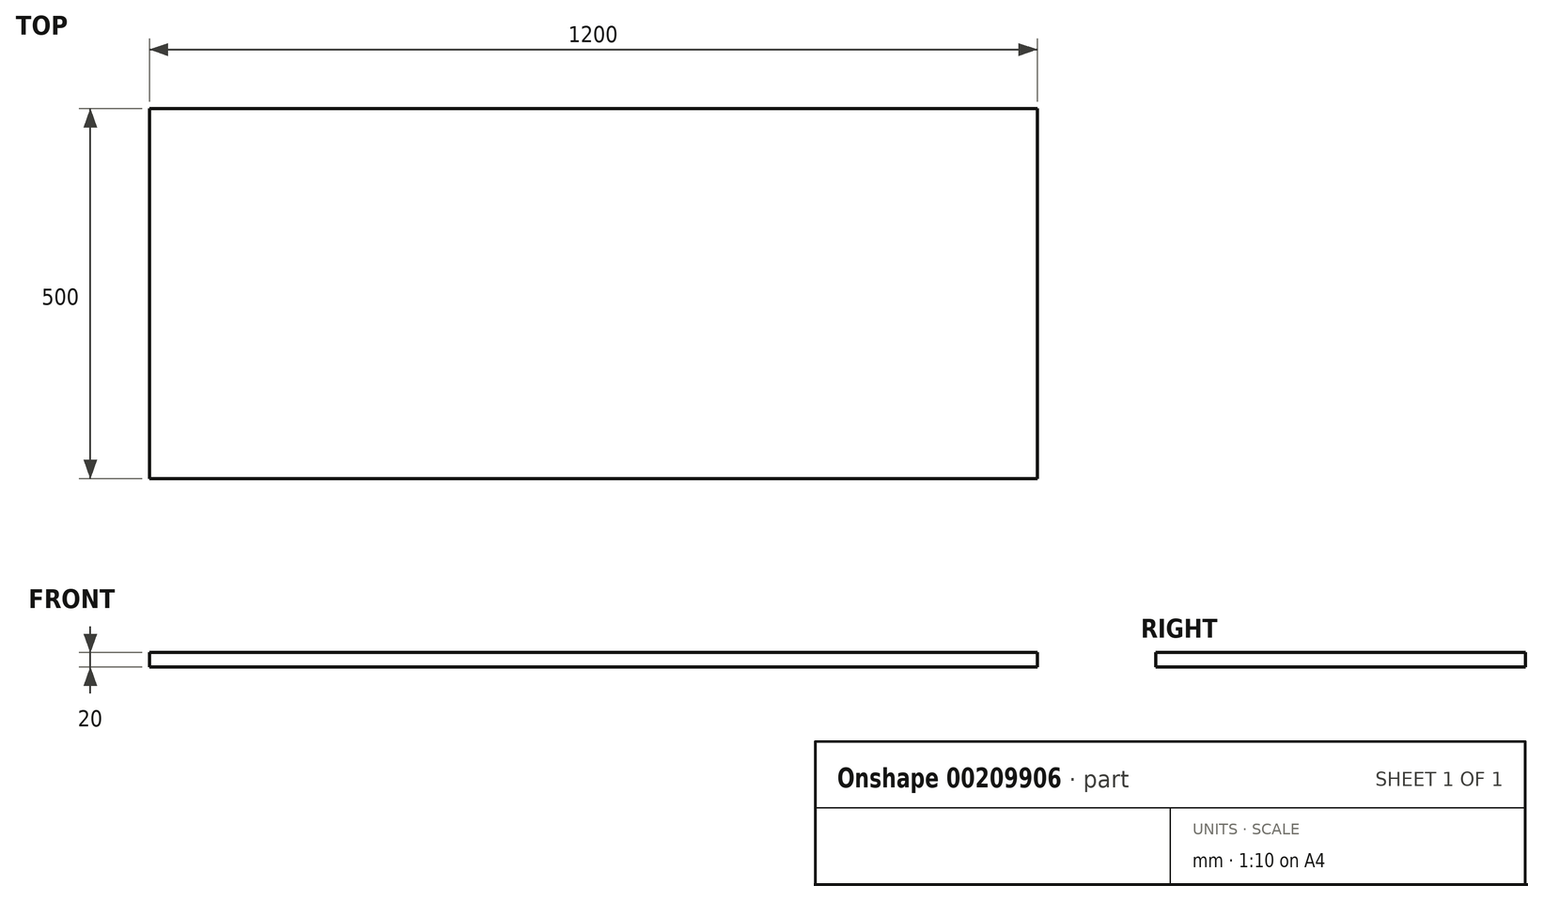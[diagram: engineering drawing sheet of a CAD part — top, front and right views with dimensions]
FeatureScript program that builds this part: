
annotation { "Feature Type Name" : "Feature", "Feature Type Description" : "" }
export const myFeature = defineFeature(function(context is Context, id is Id, definition is map)
    precondition{}
    {
        {
            var Q0;
            Q0=qCreatedBy(makeId("Top.planeOp"),FACE);
            var sketch = newSketch(context, id + "F0", { "sketchPlane" : qUnion([Q0])});
            skLineSegment(sketch, "E0.bottom", {"start": v(-600, 250) * mm, "end": v(600, 250) * mm});
            skLineSegment(sketch, "E0.top", {"start": v(-600, -250) * mm, "end": v(600, -250) * mm});
            skLineSegment(sketch, "E0.left", {"start": v(-600, 250) * mm, "end": v(-600, -250) * mm});
            skLineSegment(sketch, "E0.right", {"start": v(600, 250) * mm, "end": v(600, -250) * mm});
            skPoint(sketch, "E0.middle", {"position": v(0, 0) * mm});
            skSolve(sketch);
        }
        {
            var Q0;
            Q0=makeQuery(id+"F0.imprint","IMPRINT",FACE,{"disambiguationData":[TD([[makeQuery(id+"F0.imprint","IMPRINT",EDGE,{"derivedFrom":sQuery(id+"F0.wireOp",EDGE,"E0.bottom")}),-1.0]])]});
            extrude(context, id + "F1", {"entities" : qUnion([Q0]), "depth" : 20 * mm});
        }
    });
